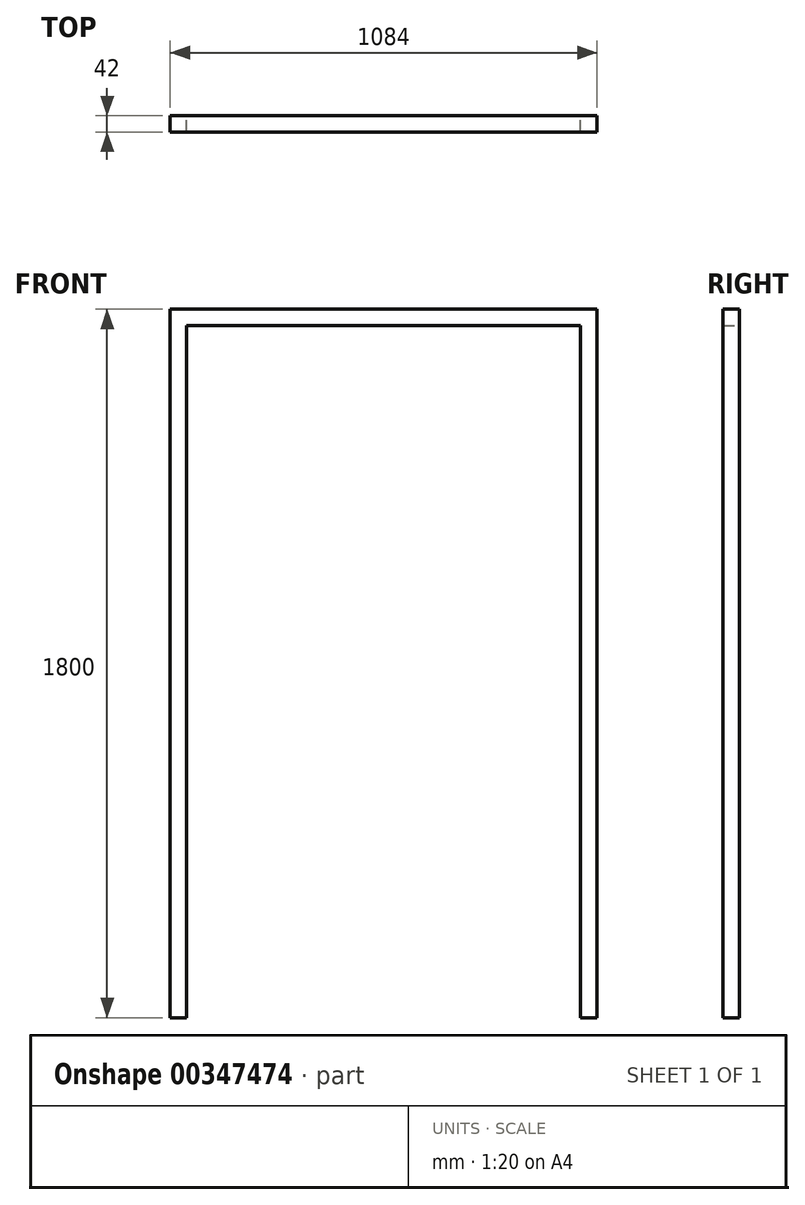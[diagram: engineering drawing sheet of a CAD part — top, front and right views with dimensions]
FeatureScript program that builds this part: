
annotation { "Feature Type Name" : "Feature", "Feature Type Description" : "" }
export const myFeature = defineFeature(function(context is Context, id is Id, definition is map)
    precondition{}
    {
        {
            var Q0;
            Q0=qCreatedBy(makeId("Top.planeOp"),FACE);
            var sketch = newSketch(context, id + "F0", { "sketchPlane" : qUnion([Q0])});
            skLineSegment(sketch, "E0.bottom", {"start": v(0, 0) * mm, "end": v(42, 0) * mm});
            skLineSegment(sketch, "E0.top", {"start": v(0, -42) * mm, "end": v(42, -42) * mm});
            skLineSegment(sketch, "E0.left", {"start": v(0, 0) * mm, "end": v(0, -42) * mm});
            skLineSegment(sketch, "E0.right", {"start": v(42, 0) * mm, "end": v(42, -42) * mm});
            skSolve(sketch);
        }
        {
            var Q0;
            Q0 = qSketchRegion(id + "F0", true);
            extrude(context, id + "F1", {"entities" : qUnion([Q0]), "depth" : 1800 * mm});
        }
        {
            var Q0;
            Q0=makeQuery(id+"F1.opExtrude","SWEPT_FACE",FACE,{"disambiguationData":[OSD([sQuery(id+"F0.wireOp",EDGE,"E0.right")])]});
            var sketch = newSketch(context, id + "F2", { "sketchPlane" : qUnion([Q0])});
            skLineSegment(sketch, "E1.bottom", {"start": v(-42, 1800) * mm, "end": v(0, 1800) * mm});
            skLineSegment(sketch, "E1.top", {"start": v(-42, 1758) * mm, "end": v(0, 1758) * mm});
            skLineSegment(sketch, "E1.left", {"start": v(-42, 1800) * mm, "end": v(-42, 1758) * mm});
            skLineSegment(sketch, "E1.right", {"start": v(0, 1800) * mm, "end": v(0, 1758) * mm});
            skSolve(sketch);
        }
        {
            var Q0;
            Q0 = qSketchRegion(id + "F2", true);
            extrude(context, id + "F3", {"entities" : qUnion([Q0]), "operationType" : NewBodyOperationType.ADD, "depth" : 1000 * mm});
        }
        {
            var Q0;
            Q0=makeQuery(id+"F3.boolean.opBoolean","MERGE",FACE,{"derivedFrom":[makeQuery(id+"F1.opExtrude","CAP_FACE",FACE,{"disambiguationData":[OSD([sQuery(id+"F0.wireOp",EDGE,"E0.bottom"),sQuery(id+"F0.wireOp",EDGE,"E0.top"),sQuery(id+"F0.wireOp",EDGE,"E0.left"),sQuery(id+"F0.wireOp",EDGE,"E0.right")])],"isStart":false}),makeQuery(id+"F3.opExtrude","SWEPT_FACE",FACE,{"disambiguationData":[OSD([sQuery(id+"F2.wireOp",EDGE,"E1.bottom")])]})]});
            var sketch = newSketch(context, id + "F4", { "sketchPlane" : qUnion([Q0])});
            skLineSegment(sketch, "E2.bottom", {"start": v(1042, 0) * mm, "end": v(1084, 0) * mm});
            skLineSegment(sketch, "E2.top", {"start": v(1042, -42) * mm, "end": v(1084, -42) * mm});
            skLineSegment(sketch, "E2.left", {"start": v(1042, 0) * mm, "end": v(1042, -42) * mm});
            skLineSegment(sketch, "E2.right", {"start": v(1084, 0) * mm, "end": v(1084, -42) * mm});
            skLineSegment(sketch, "E3.bottom", {"start": v(1063, -42) * mm, "end": v(1063, -42) * mm});
            skLineSegment(sketch, "E3.top", {"start": v(1063, -42) * mm, "end": v(1063, -42) * mm});
            skLineSegment(sketch, "E3.left", {"start": v(1063, -42) * mm, "end": v(1063, -42) * mm});
            skLineSegment(sketch, "E3.right", {"start": v(1063, -42) * mm, "end": v(1063, -42) * mm});
            skSolve(sketch);
        }
        {
            var Q0;
            Q0 = qSketchRegion(id + "F4", true);
            extrude(context, id + "F5", {"entities" : qUnion([Q0]), "operationType" : NewBodyOperationType.ADD, "oppositeDirection" : true, "depth" : 1800 * mm});
        }
    });
